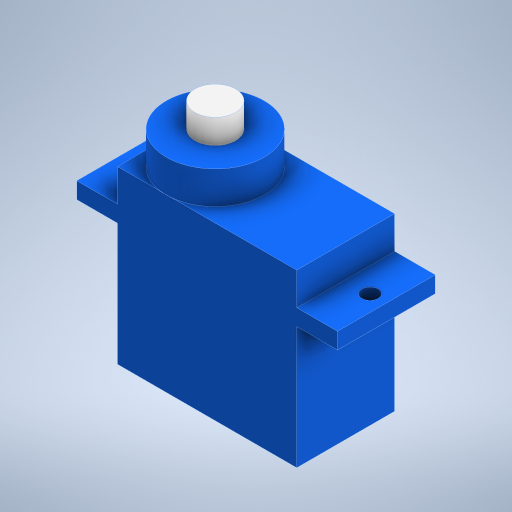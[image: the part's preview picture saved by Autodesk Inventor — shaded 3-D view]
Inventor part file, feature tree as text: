
AUTODESK INVENTOR PART (.ipt)
format: ipt  version: 2024.2 (Build 282272000, 272)  size: 303,104 bytes
history: native  units: mm
features: extrude x6, sketch x6, projected_geometry x1
ambient origin geometry x8: Origin, YZ Plane, XZ Plane, XY Plane, X Axis, Y Axis, Z Axis, Center Point
bodies: Solid1 (feature_tree)
feature tree (13):
  extrude  "Extrusion1"  Depth=12.0mm
  extrude  "Extrusion2"  Depth=5.0mm
  extrude  "Extrusion3"  Depth=2.0mm TaperAngle=0.0deg
  extrude  "Extrusion4"  Depth=12.0mm
  extrude  "Extrusion5"  Depth=5.0mm
  extrude  "Extrusion6"  Depth=2.0mm
  sketch  "Sketch1"  dims[d0=22.0mm d1=12.0mm]
  sketch  "Sketch2"  dims[d2=15.0mm d3=0.0mm d4=5.0mm]
  sketch  "Sketch3"  dims[d5=5.0mm d6=2.0mm d7=0.0mm]
  sketch  "Sketch4"  dims[d8=4.0mm d9=0.0mm d10=12.0mm]
  sketch  "Sketch5"  dims[d11=4.0mm d12=0.0mm d13=5.0mm]
  projected_geometry  "Projected Loop1"
  sketch  "Sketch6"  dims[d14=3.0mm d15=0.0mm d16=2.0mm d17=2.0mm d18=6.0mm d19=6.0mm d20=28.0mm d21=2.0mm d22=0.0mm d23=0.0mm]
